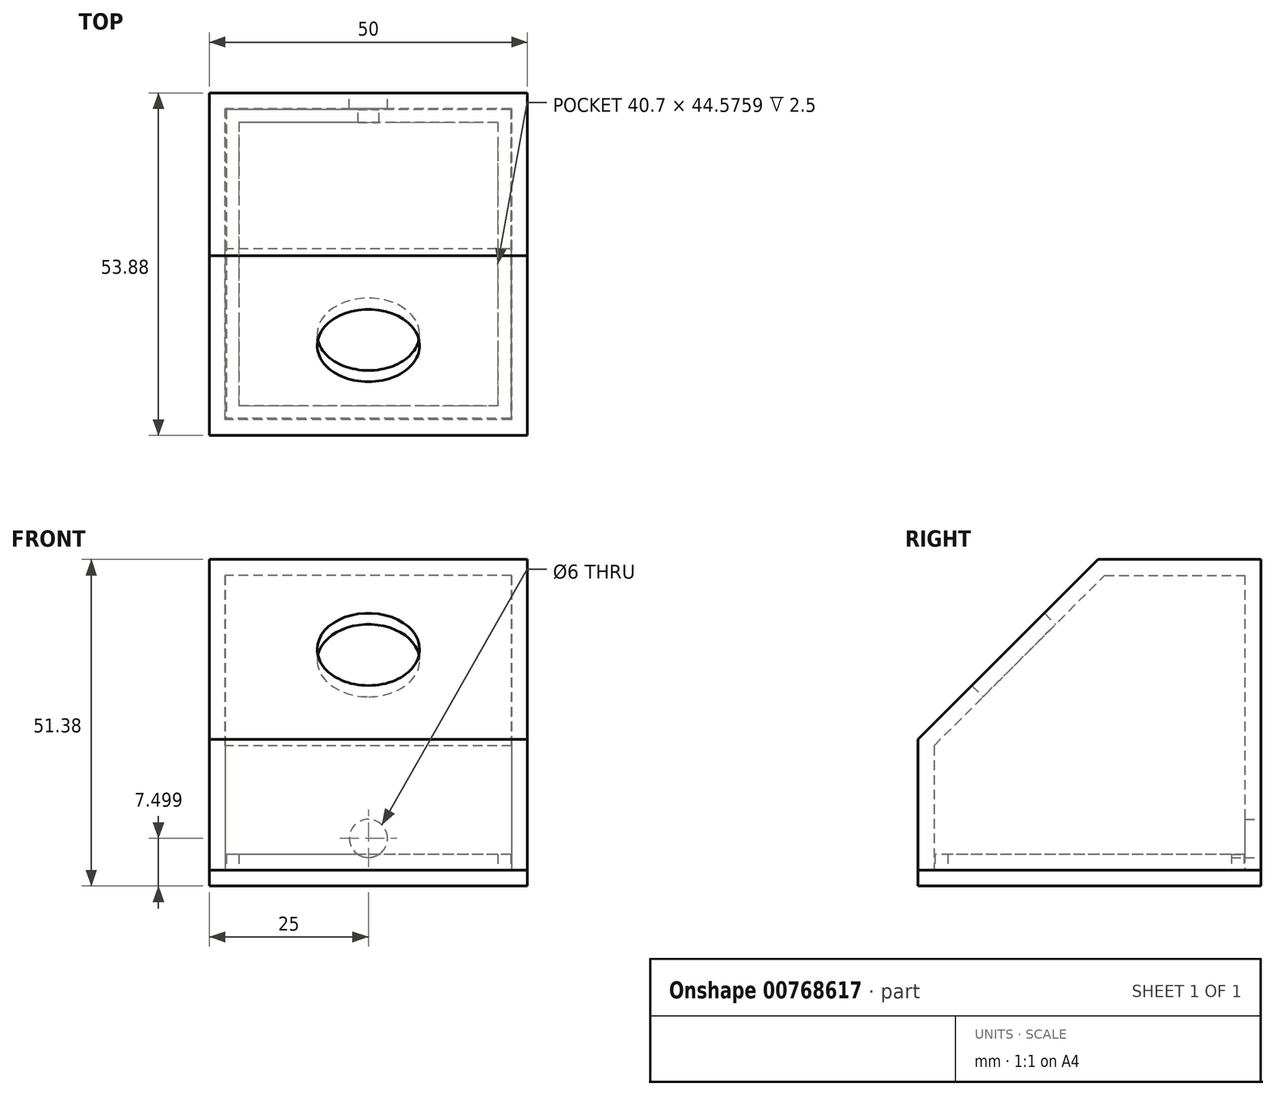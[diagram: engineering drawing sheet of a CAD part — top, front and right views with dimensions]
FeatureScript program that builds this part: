
annotation { "Feature Type Name" : "Feature", "Feature Type Description" : "" }
export const myFeature = defineFeature(function(context is Context, id is Id, definition is map)
    precondition{}
    {
        {
            var Q0;
            Q0=qCreatedBy(makeId("Right.planeOp"),FACE);
            var sketch = newSketch(context, id + "F0", { "sketchPlane" : qUnion([Q0])});
            skLineSegment(sketch, "E0", {"start": v(0, 0) * mm, "end": v(5.7, 5.7) * mm});
            skLineSegment(sketch, "E1", {"start": v(5.7, 5.7) * mm, "end": v(30.44, -19.06) * mm});
            skLineSegment(sketch, "E2", {"start": v(30.44, -19.06) * mm, "end": v(24.75, -24.75) * mm});
            skLineSegment(sketch, "E3", {"start": v(24.75, -24.75) * mm, "end": v(0, 0) * mm});
            skLineSegment(sketch, "E4", {"start": v(0, 0) * mm, "end": v(-9.1, 0) * mm, "construction": true});
            skSolve(sketch);
        }
        {
            var Q0;
            Q0=makeQuery(id+"F0.imprint","IMPRINT",FACE,{"disambiguationData":[TD([[makeQuery(id+"F0.imprint","IMPRINT",EDGE,{"derivedFrom":sQuery(id+"F0.wireOp",EDGE,"E0")}),-1.0]])]});
            var Q1;
            Q1=sQuery(id+"F0.wireOp",EDGE,"E3");
            revolve(context, id + "F1", {"surfaceOperationType" : NewSurfaceOperationType.NEW, "entities" : qUnion([Q0]), "axis" : qUnion([Q1]), "revolveType" : RevolveType.FULL});
        }
        {
            var Q0;
            Q0=qCreatedBy(makeId("Right.planeOp"),FACE);
            var sketch = newSketch(context, id + "F2", { "sketchPlane" : qUnion([Q0])});
            skLineSegment(sketch, "E5.0", {"start": v(5.7, 5.7) * mm, "end": v(-5.7, -5.7) * mm, "construction": true});
            skLineSegment(sketch, "E6", {"start": v(-13.44, -14.85) * mm, "end": v(14.85, 13.44) * mm});
            skLineSegment(sketch, "E7", {"start": v(0, 0) * mm, "end": v(0.7, -0.7) * mm, "construction": true});
            skLineSegment(sketch, "E8", {"start": v(40.44, -35.44) * mm, "end": v(-13.44, -35.44) * mm});
            skLineSegment(sketch, "E9", {"start": v(-13.44, -14.85) * mm, "end": v(-13.44, -35.44) * mm});
            skLineSegment(sketch, "E10", {"start": v(14.85, 13.44) * mm, "end": v(40.44, 13.44) * mm});
            skLineSegment(sketch, "E11", {"start": v(40.44, 13.44) * mm, "end": v(40.44, -35.44) * mm});
            skLineSegment(sketch, "E12.0", {"start": v(30.44, -19.06) * mm, "end": v(19.06, -30.44) * mm, "construction": true});
            skLineSegment(sketch, "E13.0", {"start": v(38.44, -33.44) * mm, "end": v(-11.44, -33.44) * mm});
            skLineSegment(sketch, "E13.1", {"start": v(38.44, 11.44) * mm, "end": v(38.44, -33.44) * mm});
            skLineSegment(sketch, "E13.2", {"start": v(-11.44, -15.68) * mm, "end": v(-11.44, -33.44) * mm});
            skLineSegment(sketch, "E13.3", {"start": v(-11.44, -15.68) * mm, "end": v(15.68, 11.44) * mm});
            skLineSegment(sketch, "E13.4", {"start": v(15.68, 11.44) * mm, "end": v(38.44, 11.44) * mm});
            skLineSegment(sketch, "E14", {"start": v(19.06, -30.44) * mm, "end": v(-5.7, -5.7) * mm});
            skLineSegment(sketch, "E15", {"start": v(5.7, 5.7) * mm, "end": v(30.44, -19.06) * mm});
            skSolve(sketch);
        }
        {
            var Q0;
            Q0=makeQuery(id+"F2.imprint","IMPRINT",FACE,{"disambiguationData":[TD([[makeQuery(id+"F2.imprint","IMPRINT",EDGE,{"derivedFrom":sQuery(id+"F2.wireOp",EDGE,"E8")}),-1.0]])]});
            var Q1;
            {var subQ0=sQuery(id+"F2.wireOp",EDGE,"E14");var subQ1=sQuery(id+"F2.wireOp",EDGE,"E6");var subQ2=makeQuery(id+"F2.imprint","INTERSECT",VERTEX,{"derivedFrom":[subQ1,subQ0]});Q1=makeQuery(id+"F2.imprint","IMPRINT",FACE,{"disambiguationData":[TD([[makeQuery(id+"F2.imprint","IMPRINT",EDGE,{"disambiguationData":[TD([[subQ2,-1.0]])],"derivedFrom":subQ1}),-1.0]])]});}
            var Q2;
            Q2=makeQuery(id+"F2.imprint","IMPRINT",FACE,{"disambiguationData":[TD([[makeQuery(id+"F2.imprint","IMPRINT",EDGE,{"derivedFrom":sQuery(id+"F2.wireOp",EDGE,"E13.0")}),-1.0]])]});
            extrude(context, id + "F3", {"entities" : qUnion([Q0, Q1, Q2]), "endBound" : BoundingType.SYMMETRIC, "depth" : 50 * mm, "offsetDistance" : 25 * mm});
        }
        {
            var Q0;
            Q0=makeQuery(id+"F3.opExtrude","SWEPT_FACE",FACE,{"disambiguationData":[OSD([sQuery(id+"F2.wireOp",EDGE,"E8")])]});
            shell(context, id + "F4", {"entities" : qUnion([Q0]), "thickness" : 2.5 * mm});
        }
        {
            var Q0;
            Q0=makeQuery(id+"F1.opRevolve","SWEPT_BODY",BODY,{"disambiguationData":[OSD([sQuery(id+"F0.wireOp",EDGE,"E0"),sQuery(id+"F0.wireOp",EDGE,"E1"),sQuery(id+"F0.wireOp",EDGE,"E2"),sQuery(id+"F0.wireOp",EDGE,"E3")])]});
            var Q1;
            Q1=makeQuery(id+"F3.opExtrude","SWEPT_BODY",BODY,{"disambiguationData":[OSD([sQuery(id+"F2.wireOp",EDGE,"E6"),sQuery(id+"F2.wireOp",EDGE,"E8"),sQuery(id+"F2.wireOp",EDGE,"E9"),sQuery(id+"F2.wireOp",EDGE,"E10"),sQuery(id+"F2.wireOp",EDGE,"E11")])]});
            booleanBodies(context, id + "F5", {"operationType" : BooleanOperationType.SUBTRACTION, "tools" : qUnion([Q0]), "targets" : qUnion([Q1])});
        }
        {
            var Q0;
            Q0=makeQuery(id+"F3.opExtrude","SWEPT_FACE",FACE,{"disambiguationData":[OSD([sQuery(id+"F2.wireOp",EDGE,"E8")])]});
            var sketch = newSketch(context, id + "F6", { "sketchPlane" : qUnion([Q0])});
            skLineSegment(sketch, "E16.0.0", {"start": v(-25, 13.44) * mm, "end": v(-25, -40.44) * mm});
            skLineSegment(sketch, "E16.0.1", {"start": v(-25, -40.44) * mm, "end": v(25, -40.44) * mm});
            skLineSegment(sketch, "E16.0.2", {"start": v(25, -40.44) * mm, "end": v(25, 13.44) * mm});
            skLineSegment(sketch, "E16.0.3", {"start": v(25, 13.44) * mm, "end": v(-25, 13.44) * mm});
            skSolve(sketch);
        }
        {
            var Q0;
            Q0=makeQuery(id+"F6.imprint","IMPRINT",FACE,{"disambiguationData":[TD([[makeQuery(id+"F6.imprint","IMPRINT",EDGE,{"derivedFrom":sQuery(id+"F6.wireOp",EDGE,"E16.0.0")}),-1.0]])]});
            var Q1;
            {var subQ0=sQuery(id+"F2.wireOp",EDGE,"E8");Q1=makeQuery(id+"F6.imprint","IMPRINT",FACE,{"disambiguationData":[TD([[makeQuery(id+"F6.imprint","IMPRINT",EDGE,{"derivedFrom":makeQuery(id+"F4.opShell","OFFSET_EDGE",EDGE,{"disambiguationData":[OSD([subQ0]),TDD([makeQuery(id+"F3.opExtrude","CAP_EDGE",EDGE,{"disambiguationData":[OSD([subQ0])],"isStart":true})])]})}),-1.0]])]});}
            extrude(context, id + "F7", {"entities" : qUnion([Q0, Q1]), "depth" : 2.5 * mm, "offsetDistance" : 25 * mm});
        }
        {
            var Q0;
            Q0=makeQuery(id+"F7.opExtrude","CAP_FACE",FACE,{"disambiguationData":[OSD([sQuery(id+"F6.wireOp",EDGE,"E16.0.0"),sQuery(id+"F6.wireOp",EDGE,"E16.0.1"),sQuery(id+"F6.wireOp",EDGE,"E16.0.2"),sQuery(id+"F6.wireOp",EDGE,"E16.0.3")])],"isStart":true});
            var sketch = newSketch(context, id + "F8", { "sketchPlane" : qUnion([Q0])});
            skLineSegment(sketch, "E17.0", {"start": v(22.5, 37.94) * mm, "end": v(22.5, -10.94) * mm, "construction": true});
            skLineSegment(sketch, "E18.0", {"start": v(22.5, 37.94) * mm, "end": v(-22.5, 37.94) * mm, "construction": true});
            skLineSegment(sketch, "E19.0", {"start": v(-22.5, 37.94) * mm, "end": v(-22.5, -10.94) * mm, "construction": true});
            skLineSegment(sketch, "E20.0", {"start": v(22.5, -10.94) * mm, "end": v(-22.5, -10.94) * mm, "construction": true});
            skLineSegment(sketch, "E21.0", {"start": v(-22.35, 37.8) * mm, "end": v(-22.35, -10.79) * mm});
            skLineSegment(sketch, "E21.1", {"start": v(22.35, 37.8) * mm, "end": v(-22.35, 37.8) * mm});
            skLineSegment(sketch, "E21.2", {"start": v(22.35, 37.8) * mm, "end": v(22.35, -10.79) * mm});
            skLineSegment(sketch, "E21.3", {"start": v(22.35, -10.79) * mm, "end": v(-22.35, -10.79) * mm});
            skLineSegment(sketch, "E22.0", {"start": v(20.35, 35.8) * mm, "end": v(-20.35, 35.8) * mm});
            skLineSegment(sketch, "E22.1", {"start": v(20.35, 35.8) * mm, "end": v(20.35, -8.79) * mm});
            skLineSegment(sketch, "E22.2", {"start": v(20.35, -8.79) * mm, "end": v(-20.35, -8.79) * mm});
            skLineSegment(sketch, "E22.3", {"start": v(-20.35, 35.8) * mm, "end": v(-20.35, -8.79) * mm});
            skSolve(sketch);
        }
        {
            var Q0;
            Q0=makeQuery(id+"F8.imprint","IMPRINT",FACE,{"disambiguationData":[TD([[makeQuery(id+"F8.imprint","IMPRINT",EDGE,{"derivedFrom":sQuery(id+"F8.wireOp",EDGE,"E21.0")}),1.0]])]});
            extrude(context, id + "F9", {"entities" : qUnion([Q0]), "operationType" : NewBodyOperationType.ADD, "depth" : 2.5 * mm, "offsetDistance" : 25 * mm});
        }
        {
            var Q0;
            Q0=makeQuery(id+"F3.opExtrude","SWEPT_FACE",FACE,{"disambiguationData":[OSD([sQuery(id+"F2.wireOp",EDGE,"E11")])]});
            var sketch = newSketch(context, id + "F10", { "sketchPlane" : qUnion([Q0])});
            skCircle(sketch, "E23", {"center": v(0, -30.44) * mm, "radius": 3 * mm});
            skSolve(sketch);
        }
        {
            var Q0;
            Q0=makeQuery(id+"F10.imprint","IMPRINT",FACE,{"disambiguationData":[TD([[makeQuery(id+"F10.imprint","IMPRINT",EDGE,{"derivedFrom":sQuery(id+"F10.wireOp",EDGE,"E23")}),1.0]])]});
            extrude(context, id + "F11", {"entities" : qUnion([Q0]), "operationType" : NewBodyOperationType.REMOVE, "oppositeDirection" : true, "depth" : 25 * mm, "offsetDistance" : 25 * mm});
        }
    });
